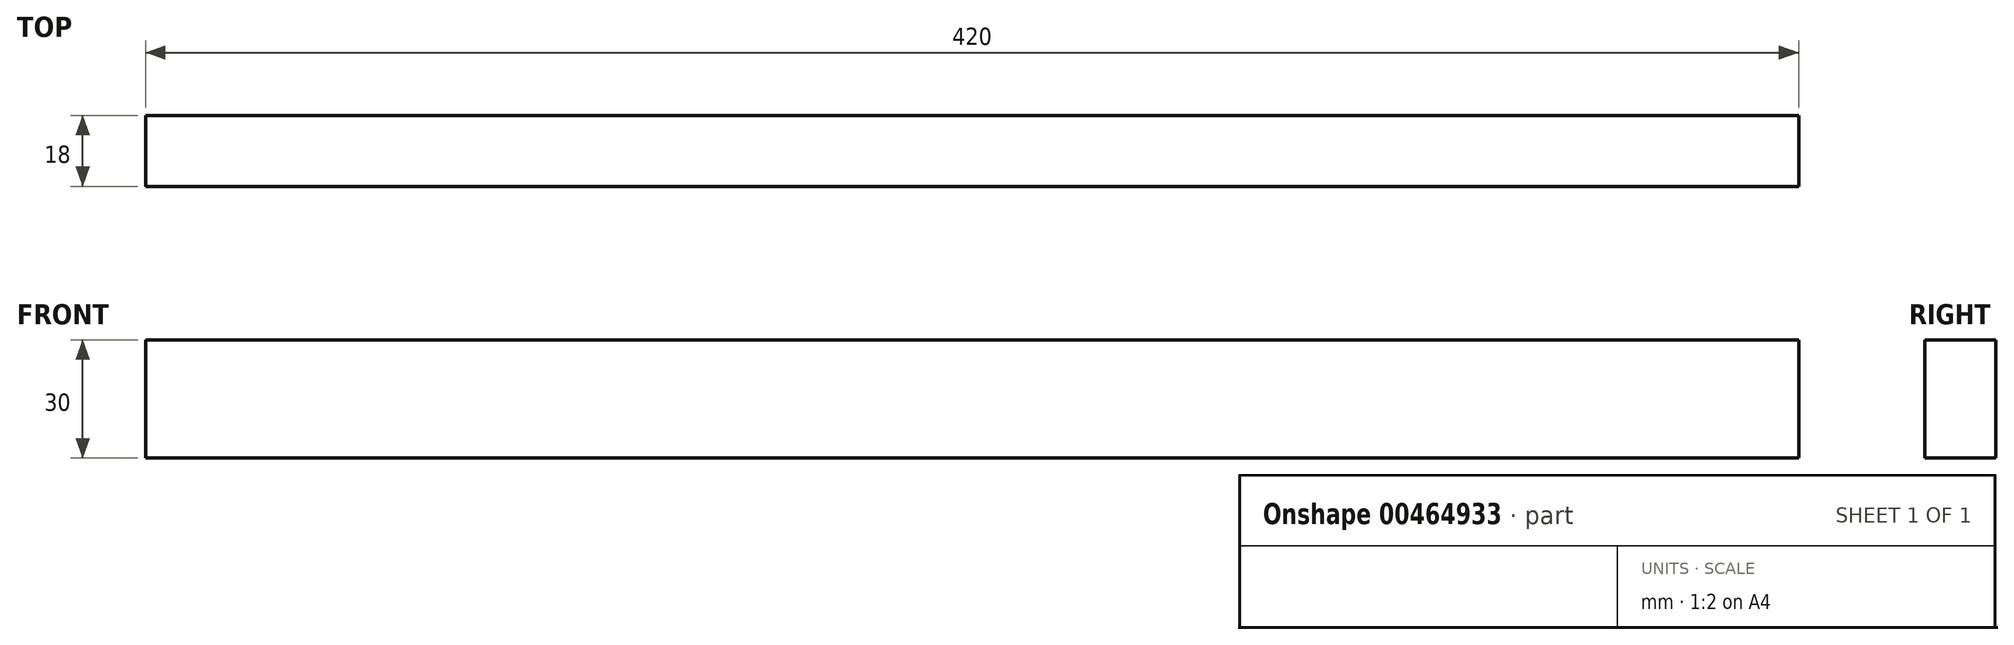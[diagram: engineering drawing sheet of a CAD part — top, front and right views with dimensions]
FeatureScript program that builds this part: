
annotation { "Feature Type Name" : "Feature", "Feature Type Description" : "" }
export const myFeature = defineFeature(function(context is Context, id is Id, definition is map)
    precondition{}
    {
        {
            var Q0;
            Q0=qCreatedBy(makeId("Right.planeOp"),FACE);
            var sketch = newSketch(context, id + "F0", { "sketchPlane" : qUnion([Q0])});
            skLineSegment(sketch, "E0.bottom", {"start": v(-9, 15) * mm, "end": v(9, 15) * mm});
            skLineSegment(sketch, "E0.top", {"start": v(-9, -15) * mm, "end": v(9, -15) * mm});
            skLineSegment(sketch, "E0.left", {"start": v(-9, 15) * mm, "end": v(-9, -15) * mm});
            skLineSegment(sketch, "E0.right", {"start": v(9, 15) * mm, "end": v(9, -15) * mm});
            skPoint(sketch, "E0.middle", {"position": v(0, 0) * mm});
            skSolve(sketch);
        }
        {
            var Q0;
            Q0=makeQuery(id+"F0.imprint","IMPRINT",FACE,{"disambiguationData":[TD([[makeQuery(id+"F0.imprint","IMPRINT",EDGE,{"derivedFrom":sQuery(id+"F0.wireOp",EDGE,"E0.bottom")}),-1.0]])]});
            extrude(context, id + "F1", {"entities" : qUnion([Q0]), "endBound" : BoundingType.SYMMETRIC, "depth" : 420 * mm, "offsetDistance" : 25 * mm});
        }
    });
